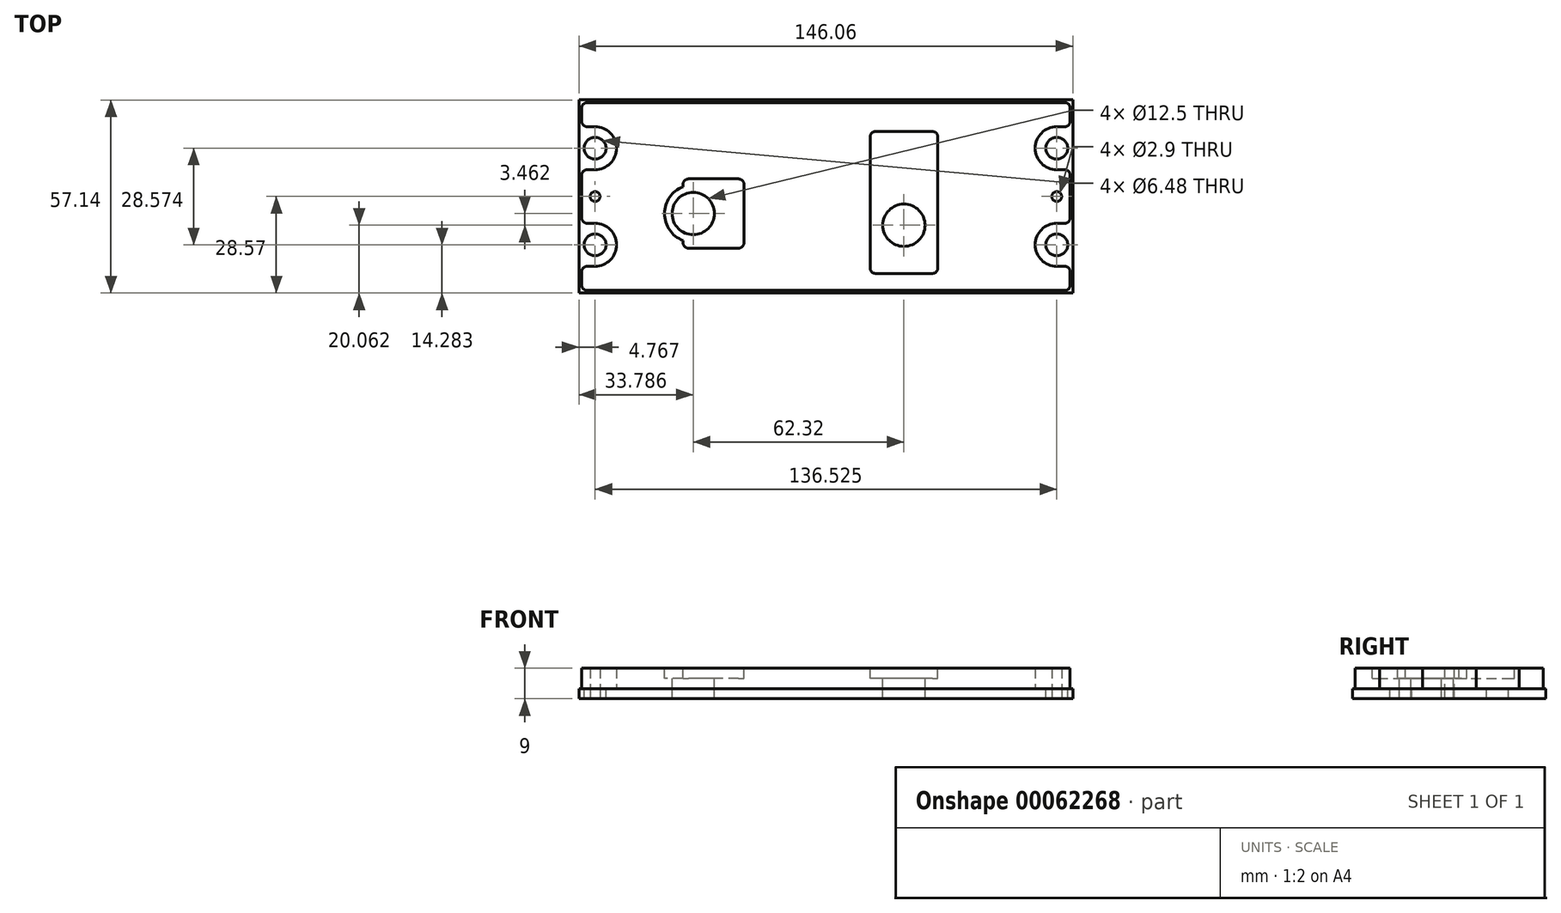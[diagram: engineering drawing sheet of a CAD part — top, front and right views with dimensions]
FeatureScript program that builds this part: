
annotation { "Feature Type Name" : "Feature", "Feature Type Description" : "" }
export const myFeature = defineFeature(function(context is Context, id is Id, definition is map)
    precondition{}
    {
        {
            var Q0;
            Q0=qCreatedBy(makeId("Top.planeOp"),FACE);
            var sketch = newSketch(context, id + "F0", { "sketchPlane" : qUnion([Q0])});
            skLineSegment(sketch, "E0.bottom", {"start": v(73.02, 28.57) * mm, "end": v(-73.03, 28.57) * mm});
            skLineSegment(sketch, "E0.top", {"start": v(73.02, -28.57) * mm, "end": v(-73.03, -28.57) * mm});
            skLineSegment(sketch, "E0.left", {"start": v(73.02, 28.57) * mm, "end": v(73.02, -28.57) * mm});
            skLineSegment(sketch, "E0.right", {"start": v(-73.03, 28.57) * mm, "end": v(-73.03, -28.57) * mm});
            skPoint(sketch, "E0.middle", {"position": v(0, 0) * mm});
            skLineSegment(sketch, "E1.bottom", {"start": v(72.22, 27.78) * mm, "end": v(-72.22, 27.78) * mm});
            skLineSegment(sketch, "E1.top", {"start": v(72.22, -27.78) * mm, "end": v(-72.22, -27.78) * mm});
            skLineSegment(sketch, "E1.left", {"start": v(72.22, 27.78) * mm, "end": v(72.22, 20.64) * mm});
            skLineSegment(sketch, "E1.right", {"start": v(-72.22, 27.78) * mm, "end": v(-72.22, 20.64) * mm});
            skArc(sketch, "E2", {"start": v(-68.26, 7.94) * mm, "mid": v(-61.91, 14.29) * mm, "end": v(-68.26, 20.64) * mm});
            skLineSegment(sketch, "E3", {"start": v(-68.26, 20.64) * mm, "end": v(-72.22, 20.64) * mm});
            skLineSegment(sketch, "E4", {"start": v(-68.26, 7.94) * mm, "end": v(-72.22, 7.94) * mm});
            skLineSegment(sketch, "E5.trimOffspring", {"start": v(-72.22, 7.94) * mm, "end": v(-72.22, -7.94) * mm});
            skCircle(sketch, "E6", {"center": v(-68.26, 14.29) * mm, "radius": 3.24 * mm});
            skLineSegment(sketch, "E7.MirrorCS", {"start": v(-68.26, -20.64) * mm, "end": v(-72.22, -20.64) * mm});
            skArc(sketch, "E8.MirrorCS", {"start": v(-68.26, -7.94) * mm, "mid": v(-61.91, -14.29) * mm, "end": v(-68.26, -20.64) * mm});
            skCircle(sketch, "E9.MirrorC", {"center": v(-68.26, -14.29) * mm, "radius": 3.24 * mm});
            skLineSegment(sketch, "E10.MirrorCS", {"start": v(-68.26, -7.94) * mm, "end": v(-72.22, -7.94) * mm});
            skLineSegment(sketch, "E11.MirrorCS", {"start": v(68.26, 7.94) * mm, "end": v(72.22, 7.94) * mm});
            skLineSegment(sketch, "E12.MirrorCS", {"start": v(68.26, 20.64) * mm, "end": v(72.22, 20.64) * mm});
            skLineSegment(sketch, "E13.MirrorCS", {"start": v(68.26, -20.64) * mm, "end": v(72.22, -20.64) * mm});
            skLineSegment(sketch, "E14.MirrorCS", {"start": v(68.26, -7.94) * mm, "end": v(72.22, -7.94) * mm});
            skCircle(sketch, "E15.MirrorC", {"center": v(68.26, 14.29) * mm, "radius": 3.24 * mm});
            skCircle(sketch, "E16.MirrorC", {"center": v(68.26, -14.29) * mm, "radius": 3.24 * mm});
            skArc(sketch, "E17.MirrorCS", {"start": v(68.26, 7.94) * mm, "mid": v(61.91, 14.29) * mm, "end": v(68.26, 20.64) * mm});
            skArc(sketch, "E18.MirrorCS", {"start": v(68.26, -7.94) * mm, "mid": v(61.91, -14.29) * mm, "end": v(68.26, -20.64) * mm});
            skLineSegment(sketch, "E19.trimOffspring", {"start": v(-72.22, -20.64) * mm, "end": v(-72.22, -27.78) * mm});
            skLineSegment(sketch, "E20.trimOffspring", {"start": v(72.22, -20.64) * mm, "end": v(72.22, -27.78) * mm});
            skLineSegment(sketch, "E21.trimOffspring", {"start": v(72.22, 7.94) * mm, "end": v(72.22, -7.94) * mm});
            skSolve(sketch);
        }
        {
            var Q0;
            Q0 = qSketchRegion(id + "F0", true);
            var Q1;
            Q1=makeQuery(id+"F0.imprint","IMPRINT",FACE,{"disambiguationData":[TD([[makeQuery(id+"F0.imprint","IMPRINT",EDGE,{"derivedFrom":sQuery(id+"F0.wireOp",EDGE,"E1.bottom")}),1.0]])]});
            extrude(context, id + "F1", {"entities" : qUnion([Q0, Q1]), "oppositeDirection" : true, "depth" : 3 * mm, "offsetDistance" : 25 * mm});
        }
        {
            var Q0;
            Q0=makeQuery(id+"F0.imprint","IMPRINT",FACE,{"disambiguationData":[TD([[makeQuery(id+"F0.imprint","IMPRINT",EDGE,{"derivedFrom":sQuery(id+"F0.wireOp",EDGE,"E1.bottom")}),1.0]])]});
            extrude(context, id + "F2", {"entities" : qUnion([Q0]), "depth" : 6 * mm, "offsetDistance" : 25 * mm});
        }
        {
            var Q0;
            Q0=makeQuery(id+"F2.opExtrude","SWEPT_EDGE",EDGE,{"disambiguationData":[OSD([sQuery(id+"F0.wireOp",EDGE,"E1.bottom"),sQuery(id+"F0.wireOp",EDGE,"E1.right")])]});
            var Q1;
            Q1=makeQuery(id+"F2.opExtrude","SWEPT_EDGE",EDGE,{"disambiguationData":[OSD([sQuery(id+"F0.wireOp",EDGE,"E1.right"),sQuery(id+"F0.wireOp",EDGE,"E3")])]});
            var Q2;
            Q2=makeQuery(id+"F2.opExtrude","SWEPT_EDGE",EDGE,{"disambiguationData":[OSD([sQuery(id+"F0.wireOp",EDGE,"E4"),sQuery(id+"F0.wireOp",EDGE,"E5.trimOffspring")])]});
            var Q3;
            Q3=makeQuery(id+"F2.opExtrude","SWEPT_EDGE",EDGE,{"disambiguationData":[OSD([sQuery(id+"F0.wireOp",EDGE,"E5.trimOffspring"),sQuery(id+"F0.wireOp",EDGE,"E10.MirrorCS")])]});
            var Q4;
            Q4=makeQuery(id+"F2.opExtrude","SWEPT_EDGE",EDGE,{"disambiguationData":[OSD([sQuery(id+"F0.wireOp",EDGE,"E7.MirrorCS"),sQuery(id+"F0.wireOp",EDGE,"E19.trimOffspring")])]});
            var Q5;
            Q5=makeQuery(id+"F2.opExtrude","SWEPT_EDGE",EDGE,{"disambiguationData":[OSD([sQuery(id+"F0.wireOp",EDGE,"E1.top"),sQuery(id+"F0.wireOp",EDGE,"E19.trimOffspring")])]});
            var Q6;
            Q6=makeQuery(id+"F2.opExtrude","SWEPT_EDGE",EDGE,{"disambiguationData":[OSD([sQuery(id+"F0.wireOp",EDGE,"E1.left"),sQuery(id+"F0.wireOp",EDGE,"E12.MirrorCS")])]});
            var Q7;
            Q7=makeQuery(id+"F2.opExtrude","SWEPT_EDGE",EDGE,{"disambiguationData":[OSD([sQuery(id+"F0.wireOp",EDGE,"E14.MirrorCS"),sQuery(id+"F0.wireOp",EDGE,"E21.trimOffspring")])]});
            var Q8;
            Q8=makeQuery(id+"F2.opExtrude","SWEPT_EDGE",EDGE,{"disambiguationData":[OSD([sQuery(id+"F0.wireOp",EDGE,"E1.top"),sQuery(id+"F0.wireOp",EDGE,"E20.trimOffspring")])]});
            var Q9;
            Q9=makeQuery(id+"F2.opExtrude","SWEPT_EDGE",EDGE,{"disambiguationData":[OSD([sQuery(id+"F0.wireOp",EDGE,"E13.MirrorCS"),sQuery(id+"F0.wireOp",EDGE,"E20.trimOffspring")])]});
            var Q10;
            Q10=makeQuery(id+"F2.opExtrude","SWEPT_EDGE",EDGE,{"disambiguationData":[OSD([sQuery(id+"F0.wireOp",EDGE,"E11.MirrorCS"),sQuery(id+"F0.wireOp",EDGE,"E21.trimOffspring")])]});
            var Q11;
            Q11=makeQuery(id+"F2.opExtrude","SWEPT_EDGE",EDGE,{"disambiguationData":[OSD([sQuery(id+"F0.wireOp",EDGE,"E1.bottom"),sQuery(id+"F0.wireOp",EDGE,"E1.left")])]});
            fillet(context, id + "F3", {"entities" : qUnion([Q0, Q1, Q2, Q3, Q4, Q5, Q6, Q7, Q8, Q9, Q10, Q11]), "radius" : 1.59 * mm, "tangentPropagation" : true, "allowEdgeOverflow" : false});
        }
        {
            var Q0;
            Q0=makeQuery(id+"F2.opExtrude","CAP_FACE",FACE,{"disambiguationData":[OSD([sQuery(id+"F0.wireOp",EDGE,"E1.bottom"),sQuery(id+"F0.wireOp",EDGE,"E1.top"),sQuery(id+"F0.wireOp",EDGE,"E1.left"),sQuery(id+"F0.wireOp",EDGE,"E1.right"),sQuery(id+"F0.wireOp",EDGE,"E2"),sQuery(id+"F0.wireOp",EDGE,"E3"),sQuery(id+"F0.wireOp",EDGE,"E4"),sQuery(id+"F0.wireOp",EDGE,"E5.trimOffspring"),sQuery(id+"F0.wireOp",EDGE,"E7.MirrorCS"),sQuery(id+"F0.wireOp",EDGE,"E8.MirrorCS"),sQuery(id+"F0.wireOp",EDGE,"E10.MirrorCS"),sQuery(id+"F0.wireOp",EDGE,"E11.MirrorCS"),sQuery(id+"F0.wireOp",EDGE,"E12.MirrorCS"),sQuery(id+"F0.wireOp",EDGE,"E13.MirrorCS"),sQuery(id+"F0.wireOp",EDGE,"E14.MirrorCS"),sQuery(id+"F0.wireOp",EDGE,"E17.MirrorCS"),sQuery(id+"F0.wireOp",EDGE,"E18.MirrorCS"),sQuery(id+"F0.wireOp",EDGE,"E19.trimOffspring"),sQuery(id+"F0.wireOp",EDGE,"E20.trimOffspring"),sQuery(id+"F0.wireOp",EDGE,"E21.trimOffspring")])],"isStart":false});
            var sketch = newSketch(context, id + "F4", { "sketchPlane" : qUnion([Q0])});
            skPoint(sketch, "E22.firstSnap0", {"position": v(-71.76, 27.3) * mm});
            skSolve(sketch);
        }
        {
            var Q0;
            {var subQ19=sQuery(id+"F0.wireOp",EDGE,"E2");Q0=makeQuery(id+"F4.imprint","IMPRINT",FACE,{"disambiguationData":[TD([[makeQuery(id+"F4.imprint","IMPRINT",EDGE,{"derivedFrom":makeQuery(id+"F2.opExtrude","CAP_EDGE",EDGE,{"disambiguationData":[OSD([subQ19])],"isStart":false})}),-1.0]])]});}
            var sketch = newSketch(context, id + "F5", { "sketchPlane" : qUnion([Q0])});
            skArc(sketch, "E23", {"start": v(-42.24, 2.9) * mm, "mid": v(-47.74, -5.05) * mm, "end": v(-42.24, -13) * mm});
            skLineSegment(sketch, "E24.bottom", {"start": v(-24.24, 5.2) * mm, "end": v(-42.24, 5.2) * mm});
            skLineSegment(sketch, "E24.top", {"start": v(-24.24, -15.3) * mm, "end": v(-42.24, -15.3) * mm});
            skLineSegment(sketch, "E24.left", {"start": v(-24.24, 5.2) * mm, "end": v(-24.24, -15.3) * mm});
            skLineSegment(sketch, "E24.right", {"start": v(-42.24, 5.2) * mm, "end": v(-42.24, 2.9) * mm});
            skLineSegment(sketch, "E25.bottom", {"start": v(33.08, -22.76) * mm, "end": v(13.08, -22.76) * mm});
            skLineSegment(sketch, "E25.top", {"start": v(33.08, 19.24) * mm, "end": v(13.08, 19.24) * mm});
            skLineSegment(sketch, "E25.left", {"start": v(33.08, -22.76) * mm, "end": v(33.08, 19.24) * mm});
            skLineSegment(sketch, "E25.right", {"start": v(13.08, -22.76) * mm, "end": v(13.08, 19.24) * mm});
            skCircle(sketch, "E26", {"center": v(23.08, -8.5) * mm, "radius": 6.25 * mm});
            skPoint(sketch, "E26.centerSnap0", {"position": v(23.08, -22.76) * mm});
            skCircle(sketch, "E27", {"center": v(-39.24, -5.05) * mm, "radius": 6.25 * mm});
            skPoint(sketch, "E28", {"position": v(-24.24, -5.05) * mm});
            skLineSegment(sketch, "E29", {"start": v(-42.24, -13) * mm, "end": v(-42.24, -15.3) * mm});
            skSolve(sketch);
        }
        {
            var Q0;
            Q0=makeQuery(id+"F5.imprint","IMPRINT",FACE,{"disambiguationData":[TD([[makeQuery(id+"F5.imprint","IMPRINT",EDGE,{"derivedFrom":sQuery(id+"F5.wireOp",EDGE,"E25.bottom")}),-1.0]])]});
            var Q1;
            Q1=makeQuery(id+"F5.imprint","IMPRINT",FACE,{"disambiguationData":[TD([[makeQuery(id+"F5.imprint","IMPRINT",EDGE,{"derivedFrom":sQuery(id+"F5.wireOp",EDGE,"E23")}),1.0]])]});
            extrude(context, id + "F6", {"entities" : qUnion([Q0, Q1]), "operationType" : NewBodyOperationType.REMOVE, "oppositeDirection" : true, "depth" : 3 * mm, "offsetDistance" : 25 * mm});
        }
        {
            var Q0;
            Q0=makeQuery(id+"F5.imprint","IMPRINT",FACE,{"disambiguationData":[TD([[makeQuery(id+"F5.imprint","IMPRINT",EDGE,{"derivedFrom":sQuery(id+"F5.wireOp",EDGE,"E26")}),1.0]])]});
            var Q1;
            Q1=makeQuery(id+"F5.imprint","IMPRINT",FACE,{"disambiguationData":[TD([[makeQuery(id+"F5.imprint","IMPRINT",EDGE,{"derivedFrom":sQuery(id+"F5.wireOp",EDGE,"E27")}),1.0]])]});
            extrude(context, id + "F7", {"entities" : qUnion([Q0, Q1]), "operationType" : NewBodyOperationType.REMOVE, "oppositeDirection" : true, "depth" : 25 * mm, "offsetDistance" : 25 * mm});
        }
        {
            var Q0;
            Q0=makeQuery(id+"F6.boolean.opBoolean","COPY",EDGE,{"derivedFrom":makeQuery(id+"F6.opExtrude","SWEPT_EDGE",EDGE,{"disambiguationData":[OSD([sQuery(id+"F5.wireOp",EDGE,"E24.bottom"),sQuery(id+"F5.wireOp",EDGE,"E24.right")])]})});
            var Q1;
            Q1=makeQuery(id+"F6.boolean.opBoolean","COPY",EDGE,{"derivedFrom":makeQuery(id+"F6.opExtrude","SWEPT_EDGE",EDGE,{"disambiguationData":[OSD([sQuery(id+"F5.wireOp",EDGE,"E24.bottom"),sQuery(id+"F5.wireOp",EDGE,"E24.left")])]})});
            var Q2;
            Q2=makeQuery(id+"F6.boolean.opBoolean","COPY",EDGE,{"derivedFrom":makeQuery(id+"F6.opExtrude","SWEPT_EDGE",EDGE,{"disambiguationData":[OSD([sQuery(id+"F5.wireOp",EDGE,"E24.top"),sQuery(id+"F5.wireOp",EDGE,"E24.left")])]})});
            var Q3;
            Q3=makeQuery(id+"F6.boolean.opBoolean","COPY",EDGE,{"derivedFrom":makeQuery(id+"F6.opExtrude","SWEPT_EDGE",EDGE,{"disambiguationData":[OSD([sQuery(id+"F5.wireOp",EDGE,"E24.top"),sQuery(id+"F5.wireOp",EDGE,"d4120456-72d0-45c4-b862-c14f243d580c.trimOffspring")])]})});
            var Q4;
            Q4=makeQuery(id+"F6.boolean.opBoolean","COPY",EDGE,{"derivedFrom":makeQuery(id+"F6.opExtrude","SWEPT_EDGE",EDGE,{"disambiguationData":[OSD([sQuery(id+"F5.wireOp",EDGE,"E25.top"),sQuery(id+"F5.wireOp",EDGE,"E25.right")])]})});
            var Q5;
            Q5=makeQuery(id+"F6.boolean.opBoolean","COPY",EDGE,{"derivedFrom":makeQuery(id+"F6.opExtrude","SWEPT_EDGE",EDGE,{"disambiguationData":[OSD([sQuery(id+"F5.wireOp",EDGE,"E25.top"),sQuery(id+"F5.wireOp",EDGE,"E25.left")])]})});
            var Q6;
            Q6=makeQuery(id+"F6.boolean.opBoolean","COPY",EDGE,{"derivedFrom":makeQuery(id+"F6.opExtrude","SWEPT_EDGE",EDGE,{"disambiguationData":[OSD([sQuery(id+"F5.wireOp",EDGE,"E25.bottom"),sQuery(id+"F5.wireOp",EDGE,"E25.right")])]})});
            var Q7;
            Q7=makeQuery(id+"F6.boolean.opBoolean","COPY",EDGE,{"derivedFrom":makeQuery(id+"F6.opExtrude","SWEPT_EDGE",EDGE,{"disambiguationData":[OSD([sQuery(id+"F5.wireOp",EDGE,"E25.bottom"),sQuery(id+"F5.wireOp",EDGE,"E25.left")])]})});
            fillet(context, id + "F8", {"entities" : qUnion([Q0, Q1, Q2, Q3, Q4, Q5, Q6, Q7]), "radius" : 1.59 * mm, "tangentPropagation" : true, "allowEdgeOverflow" : false});
        }
        {
            var Q0;
            {var subQ0=sQuery(id+"F0.wireOp",EDGE,"E21.trimOffspring");var subQ1=sQuery(id+"F0.wireOp",EDGE,"E20.trimOffspring");var subQ2=sQuery(id+"F0.wireOp",EDGE,"E19.trimOffspring");var subQ3=sQuery(id+"F0.wireOp",EDGE,"E18.MirrorCS");var subQ4=sQuery(id+"F0.wireOp",EDGE,"E17.MirrorCS");var subQ5=sQuery(id+"F0.wireOp",EDGE,"E14.MirrorCS");var subQ6=sQuery(id+"F0.wireOp",EDGE,"E13.MirrorCS");var subQ7=sQuery(id+"F0.wireOp",EDGE,"E12.MirrorCS");var subQ8=sQuery(id+"F0.wireOp",EDGE,"E11.MirrorCS");var subQ9=sQuery(id+"F0.wireOp",EDGE,"E10.MirrorCS");var subQ10=sQuery(id+"F0.wireOp",EDGE,"E1.left");var subQ11=sQuery(id+"F0.wireOp",EDGE,"E1.top");var subQ12=sQuery(id+"F0.wireOp",EDGE,"E1.right");var subQ13=sQuery(id+"F0.wireOp",EDGE,"E1.bottom");var subQ14=sQuery(id+"F0.wireOp",EDGE,"E8.MirrorCS");var subQ15=sQuery(id+"F0.wireOp",EDGE,"E2");var subQ16=sQuery(id+"F0.wireOp",EDGE,"E3");var subQ17=sQuery(id+"F0.wireOp",EDGE,"E4");var subQ18=sQuery(id+"F0.wireOp",EDGE,"E5.trimOffspring");var subQ19=sQuery(id+"F0.wireOp",EDGE,"E7.MirrorCS");Q0=makeQuery(id+"F6.boolean.opBoolean","SPLIT",FACE,{"disambiguationData":[TD([makeQuery(id+"F2.opExtrude","SWEPT_FACE",FACE,{"disambiguationData":[OSD([subQ13])]})])],"derivedFrom":makeQuery(id+"F2.opExtrude","CAP_FACE",FACE,{"disambiguationData":[OSD([subQ13,subQ11,subQ10,subQ12,subQ15,subQ16,subQ17,subQ18,subQ19,subQ14,subQ9,subQ8,subQ7,subQ6,subQ5,subQ4,subQ3,subQ2,subQ1,subQ0])],"isStart":false})});}
            var sketch = newSketch(context, id + "F9", { "sketchPlane" : qUnion([Q0])});
            skPoint(sketch, "E30", {"position": v(-68.26, 0) * mm});
            skPoint(sketch, "E31", {"position": v(68.26, 0) * mm});
            skSolve(sketch);
        }
        {
            var Q0;
            Q0=sQuery(id+"F9.wireOp",VERTEX,"E30");
            var Q1;
            Q1=sQuery(id+"F9.wireOp",VERTEX,"E31");
            var Q2;
            Q2=makeQuery(id+"F2.opExtrude","SWEPT_BODY",BODY,{"disambiguationData":[OSD([sQuery(id+"F0.wireOp",EDGE,"E1.bottom"),sQuery(id+"F0.wireOp",EDGE,"E1.top"),sQuery(id+"F0.wireOp",EDGE,"E1.left"),sQuery(id+"F0.wireOp",EDGE,"E1.right"),sQuery(id+"F0.wireOp",EDGE,"E2"),sQuery(id+"F0.wireOp",EDGE,"E3"),sQuery(id+"F0.wireOp",EDGE,"E4"),sQuery(id+"F0.wireOp",EDGE,"E5.trimOffspring"),sQuery(id+"F0.wireOp",EDGE,"E7.MirrorCS"),sQuery(id+"F0.wireOp",EDGE,"E8.MirrorCS"),sQuery(id+"F0.wireOp",EDGE,"E10.MirrorCS"),sQuery(id+"F0.wireOp",EDGE,"E11.MirrorCS"),sQuery(id+"F0.wireOp",EDGE,"E12.MirrorCS"),sQuery(id+"F0.wireOp",EDGE,"E13.MirrorCS"),sQuery(id+"F0.wireOp",EDGE,"E14.MirrorCS"),sQuery(id+"F0.wireOp",EDGE,"E17.MirrorCS"),sQuery(id+"F0.wireOp",EDGE,"E18.MirrorCS"),sQuery(id+"F0.wireOp",EDGE,"E19.trimOffspring"),sQuery(id+"F0.wireOp",EDGE,"E20.trimOffspring"),sQuery(id+"F0.wireOp",EDGE,"E21.trimOffspring")])]});
            var Q3;
            Q3=makeQuery(id+"F1.opExtrude","SWEPT_BODY",BODY,{"disambiguationData":[OSD([sQuery(id+"F0.wireOp",EDGE,"E0.bottom"),sQuery(id+"F0.wireOp",EDGE,"E0.top"),sQuery(id+"F0.wireOp",EDGE,"E0.left"),sQuery(id+"F0.wireOp",EDGE,"E0.right"),sQuery(id+"F0.wireOp",EDGE,"E6"),sQuery(id+"F0.wireOp",EDGE,"E9.MirrorC"),sQuery(id+"F0.wireOp",EDGE,"E15.MirrorC"),sQuery(id+"F0.wireOp",EDGE,"E16.MirrorC")])]});
            hole(context, id + "F10", {"style" : HoleStyle.SIMPLE, "endStyle" : HoleEndStyle.BLIND, "holeDiameter" : 2.9 * mm, "majorDiameter" : 5 * mm, "holeDepth" : 10 * mm, "isTappedThrough" : true, "tappedDepth" : 12 * mm, "tapClearance" : 3, "locations" : qUnion([Q0, Q1]), "scope" : qUnion([Q2, Q3])});
        }
    });
